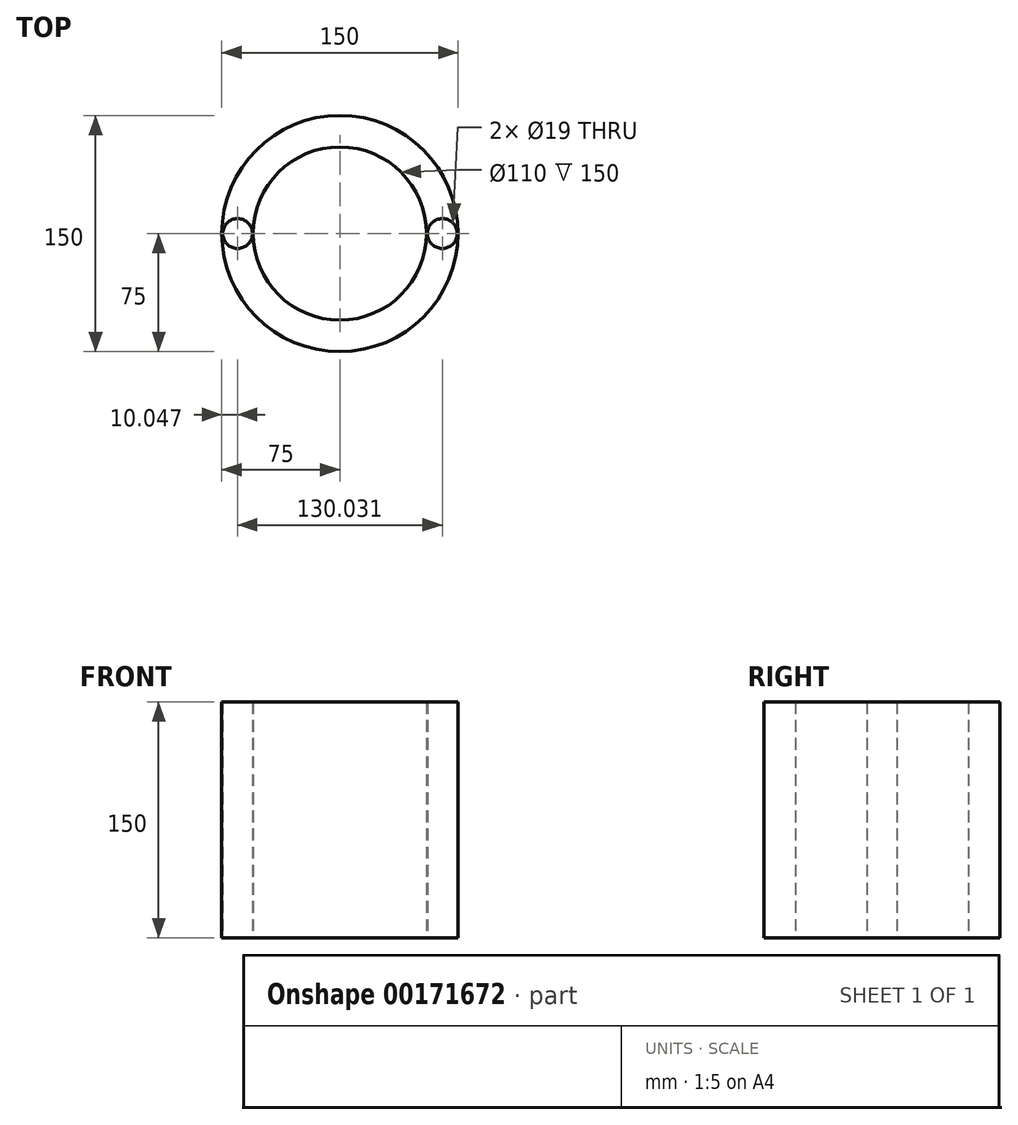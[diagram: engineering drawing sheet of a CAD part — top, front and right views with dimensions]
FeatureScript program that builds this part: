
annotation { "Feature Type Name" : "Feature", "Feature Type Description" : "" }
export const myFeature = defineFeature(function(context is Context, id is Id, definition is map)
    precondition{}
    {
        {
            var Q0;
            Q0=qCreatedBy(makeId("Top.planeOp"),FACE);
            var sketch = newSketch(context, id + "F0", { "sketchPlane" : qUnion([Q0])});
            skCircle(sketch, "E0", {"center": v(0, 0) * mm, "radius": 55 * mm});
            skCircle(sketch, "E1", {"center": v(0, 0) * mm, "radius": 75 * mm});
            skCircle(sketch, "E2", {"center": v(-64.95, 0) * mm, "radius": 9.5 * mm});
            skCircle(sketch, "E3", {"center": v(65.08, 0) * mm, "radius": 9.5 * mm});
            skCircle(sketch, "E4", {"center": v(-64.95, 0) * mm, "radius": 8.5 * mm});
            skCircle(sketch, "E5", {"center": v(65.08, 0) * mm, "radius": 8.5 * mm});
            skSolve(sketch);
        }
        {
            var Q0;
            Q0=makeQuery(id+"F0.imprint","IMPRINT",FACE,{"disambiguationData":[TD([[makeQuery(id+"F0.imprint","IMPRINT",EDGE,{"derivedFrom":sQuery(id+"F0.wireOp",EDGE,"E1")}),1.0]])]});
            extrude(context, id + "F1", {"entities" : qUnion([Q0]), "depth" : 150 * mm});
        }
    });
